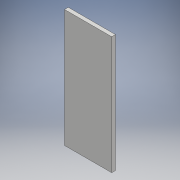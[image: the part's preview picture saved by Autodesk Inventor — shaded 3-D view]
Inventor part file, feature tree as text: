
AUTODESK INVENTOR PART (.ipt)
format: ipt  version: 2018 (Build 220112000, 112)  size: 90,624 bytes
history: native  units: mm
features: extrude x1, sketch x1
ambient origin geometry x8: Origin, YZ Plane, XZ Plane, XY Plane, X Axis, Y Axis, Z Axis, Center Point
bodies: Solid1 (feature_tree)
feature tree (2):
  extrude  "Extrusion1"  Depth=50.0mm
  sketch  "Sketch1"  dims[d0=20.0mm d1=50.0mm d2=1.6mm d3=0.0mm]
